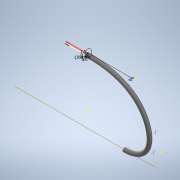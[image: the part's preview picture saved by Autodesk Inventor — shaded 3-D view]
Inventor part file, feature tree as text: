
AUTODESK INVENTOR PART (.ipt)
format: ipt  version: 2021 (Build 250183000, 183)  size: 219,648 bytes
history: native  units: mm
features: other x14, sketch x8, extrude x2, reference x2, sweep x1
ambient origin geometry x8: Origin, YZ Plane, XZ Plane, XY Plane, X Axis, Y Axis, Z Axis, Center Point
bodies: Body1 (feature_tree)
feature tree (27):
  other  "Bryła1"
  other  "Płaszczyzna konstrukcyjna1"
  sketch  "Szkic1"
  sketch  "Szkic 3D1"
  other  "Oś konstrukcyjna1"
  other  "Płaszczyzna konstrukcyjna4"
  sketch  "Szkic3"
  other  "Płaszczyzna konstrukcyjna5"
  other  "Płaszczyzna konstrukcyjna7"
  other  "Płaszczyzna konstrukcyjna8"
  other  "Płaszczyzna konstrukcyjna9"
  sketch  "Szkic5"
  sketch  "Szkic6"
  sketch  "Szkic 3D3"
  other  "Płaszczyzna konstrukcyjna11"
  sweep  "Przeciągnięcie1"
  sketch  "Szkic8"
  extrude  "Wyciągnięcie proste1"  Depth=2.5mm
  extrude  "Wyciągnięcie proste2"  Depth=2.0mm
  reference  "Odniesienie1"
  other  "Płaszczyzna konstrukcyjna10"
  sketch  "Szkic7"
  reference  "Odniesienie4"
  parser-record x1  (decoder bookkeeping rows leaked as tree rows — omitted from the tree; the rows remain in map.json)
  other  "model tensometru.iam"
  other  "kabelki:1"
  other  "podstwa:1"
note: 1 file-system path scrubbed to <path> (originals preserved in map.json)
